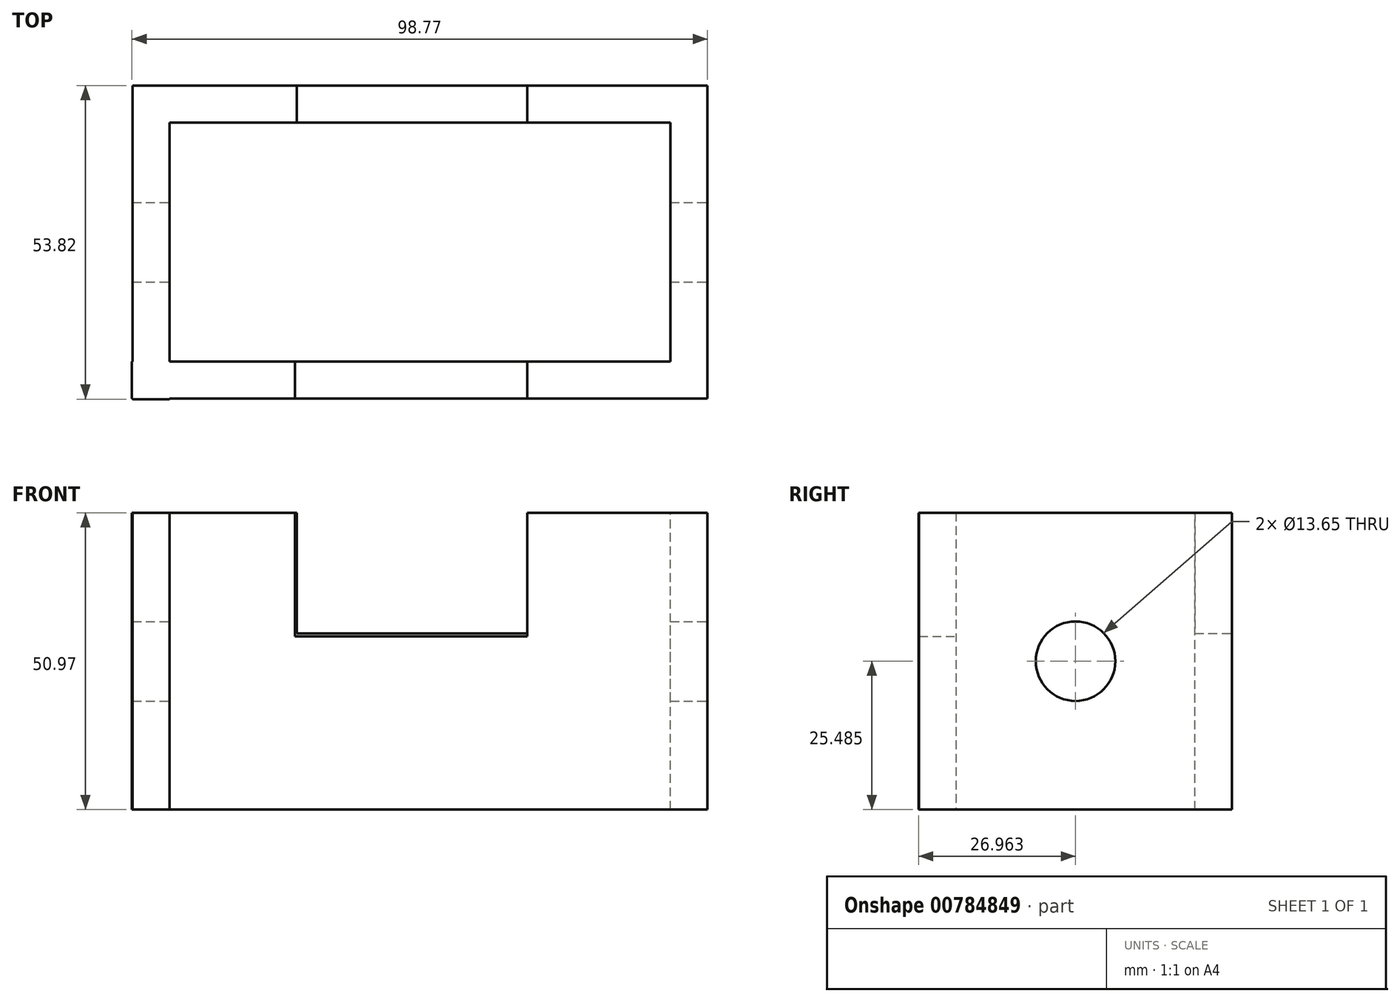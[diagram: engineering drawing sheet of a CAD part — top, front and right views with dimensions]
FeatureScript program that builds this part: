
annotation { "Feature Type Name" : "Feature", "Feature Type Description" : "" }
export const myFeature = defineFeature(function(context is Context, id is Id, definition is map)
    precondition{}
    {
        {
            var Q0;
            Q0=qCreatedBy(makeId("Front.planeOp"),FACE);
            var sketch = newSketch(context, id + "F0", { "sketchPlane" : qUnion([Q0])});
            skLineSegment(sketch, "E0", {"start": v(-50.35, 50.97) * mm, "end": v(-50.35, 0) * mm});
            skLineSegment(sketch, "E1", {"start": v(48.42, 50.97) * mm, "end": v(48.42, 0) * mm});
            skLineSegment(sketch, "E2", {"start": v(48.42, 0) * mm, "end": v(-50.35, 0) * mm});
            skLineSegment(sketch, "E3", {"start": v(-50.35, 50.97) * mm, "end": v(-28.88, 50.97) * mm});
            skLineSegment(sketch, "E4", {"start": v(25.48, 50.97) * mm, "end": v(48.42, 50.97) * mm});
            skLineSegment(sketch, "E5", {"start": v(-28.88, 50.97) * mm, "end": v(-22.4, 50.97) * mm});
            skLineSegment(sketch, "E6", {"start": v(-22.4, 50.97) * mm, "end": v(-22.4, 29.77) * mm});
            skLineSegment(sketch, "E7", {"start": v(-22.4, 29.77) * mm, "end": v(17.47, 29.77) * mm});
            skLineSegment(sketch, "E8", {"start": v(17.47, 29.77) * mm, "end": v(17.47, 50.97) * mm});
            skLineSegment(sketch, "E9", {"start": v(17.47, 50.97) * mm, "end": v(25.48, 50.97) * mm});
            skSolve(sketch);
        }
        {
            var Q0;
            Q0 = qSketchRegion(id + "F0", true);
            extrude(context, id + "F1", {"entities" : qUnion([Q0]), "depth" : 6.35 * mm, "offsetDistance" : 25.4 * mm});
        }
        {
            var Q0;
            Q0=makeQuery(id+"F1.opExtrude","SWEPT_FACE",FACE,{"disambiguationData":[OSD([sQuery(id+"F0.wireOp",EDGE,"E1")])]});
            var sketch = newSketch(context, id + "F2", { "sketchPlane" : qUnion([Q0])});
            skLineSegment(sketch, "E10.bottom", {"start": v(-6.35, 50.97) * mm, "end": v(47.36, 50.97) * mm});
            skLineSegment(sketch, "E10.top", {"start": v(-6.35, 0) * mm, "end": v(47.36, 0) * mm});
            skLineSegment(sketch, "E10.left", {"start": v(-6.35, 50.97) * mm, "end": v(-6.35, 0) * mm});
            skLineSegment(sketch, "E10.right", {"start": v(47.36, 50.97) * mm, "end": v(47.36, 0) * mm});
            skSolve(sketch);
        }
        {
            var Q0;
            Q0 = qSketchRegion(id + "F2", true);
            extrude(context, id + "F3", {"entities" : qUnion([Q0]), "operationType" : NewBodyOperationType.ADD, "oppositeDirection" : true, "depth" : 6.35 * mm, "offsetDistance" : 25.4 * mm});
        }
        {
            var Q0;
            Q0=makeQuery(id+"F3.opExtrude","SWEPT_FACE",FACE,{"disambiguationData":[OSD([sQuery(id+"F2.wireOp",EDGE,"E10.right")])]});
            var sketch = newSketch(context, id + "F4", { "sketchPlane" : qUnion([Q0])});
            skLineSegment(sketch, "E11", {"start": v(-48.42, 50.97) * mm, "end": v(-17.47, 50.97) * mm});
            skLineSegment(sketch, "E12", {"start": v(-17.47, 50.97) * mm, "end": v(-17.47, 30.24) * mm});
            skLineSegment(sketch, "E13", {"start": v(-17.47, 30.24) * mm, "end": v(22.05, 30.24) * mm});
            skLineSegment(sketch, "E14", {"start": v(22.05, 30.24) * mm, "end": v(22.05, 50.97) * mm});
            skLineSegment(sketch, "E15", {"start": v(22.05, 50.97) * mm, "end": v(50.25, 50.97) * mm});
            skLineSegment(sketch, "E16", {"start": v(50.25, 50.97) * mm, "end": v(50.25, 0) * mm});
            skLineSegment(sketch, "E17", {"start": v(50.25, 0) * mm, "end": v(-48.42, 0) * mm});
            skLineSegment(sketch, "E18", {"start": v(-48.42, 0) * mm, "end": v(-48.42, 50.97) * mm});
            skSolve(sketch);
        }
        {
            var Q0;
            Q0 = qSketchRegion(id + "F4", true);
            extrude(context, id + "F5", {"entities" : qUnion([Q0]), "operationType" : NewBodyOperationType.ADD, "oppositeDirection" : true, "depth" : 6.35 * mm, "offsetDistance" : 25.4 * mm});
        }
        {
            var Q0;
            Q0=makeQuery(id+"F5.opExtrude","SWEPT_FACE",FACE,{"disambiguationData":[OSD([sQuery(id+"F4.wireOp",EDGE,"E16")])]});
            var sketch = newSketch(context, id + "F6", { "sketchPlane" : qUnion([Q0])});
            skLineSegment(sketch, "E19.bottom", {"start": v(-47.36, 50.97) * mm, "end": v(6.46, 50.97) * mm});
            skLineSegment(sketch, "E19.top", {"start": v(-47.36, 0) * mm, "end": v(6.46, 0) * mm});
            skLineSegment(sketch, "E19.left", {"start": v(-47.36, 50.97) * mm, "end": v(-47.36, 0) * mm});
            skLineSegment(sketch, "E19.right", {"start": v(6.46, 50.97) * mm, "end": v(6.46, 0) * mm});
            skSolve(sketch);
        }
        {
            var Q0;
            Q0 = qSketchRegion(id + "F6", true);
            extrude(context, id + "F7", {"entities" : qUnion([Q0]), "operationType" : NewBodyOperationType.ADD, "oppositeDirection" : true, "depth" : 6.35 * mm, "offsetDistance" : 25.4 * mm});
        }
        {
            var Q0;
            Q0=makeQuery(id+"F3.boolean.opBoolean","MERGE",FACE,{"derivedFrom":[makeQuery(id+"F1.opExtrude","SWEPT_FACE",FACE,{"disambiguationData":[OSD([sQuery(id+"F0.wireOp",EDGE,"E1")])]}),makeQuery(id+"F3.opExtrude","CAP_FACE",FACE,{"disambiguationData":[OSD([sQuery(id+"F2.wireOp",EDGE,"E10.bottom"),sQuery(id+"F2.wireOp",EDGE,"E10.top"),sQuery(id+"F2.wireOp",EDGE,"E10.left"),sQuery(id+"F2.wireOp",EDGE,"E10.right")])],"isStart":true})]});
            var sketch = newSketch(context, id + "F8", { "sketchPlane" : qUnion([Q0])});
            skCircle(sketch, "E20", {"center": v(20.5, 25.49) * mm, "radius": 6.83 * mm});
            skPoint(sketch, "E20.centerSnap0", {"position": v(47.36, 25.49) * mm});
            skPoint(sketch, "E20.centerSnap1", {"position": v(20.5, 50.97) * mm});
            skSolve(sketch);
        }
        {
            var Q0;
            Q0 = qSketchRegion(id + "F8", true);
            extrude(context, id + "F9", {"entities" : qUnion([Q0]), "operationType" : NewBodyOperationType.REMOVE, "endBound" : BoundingType.THROUGH_ALL, "oppositeDirection" : true, "depth" : 25.4 * mm, "offsetDistance" : 25.4 * mm});
        }
    });
